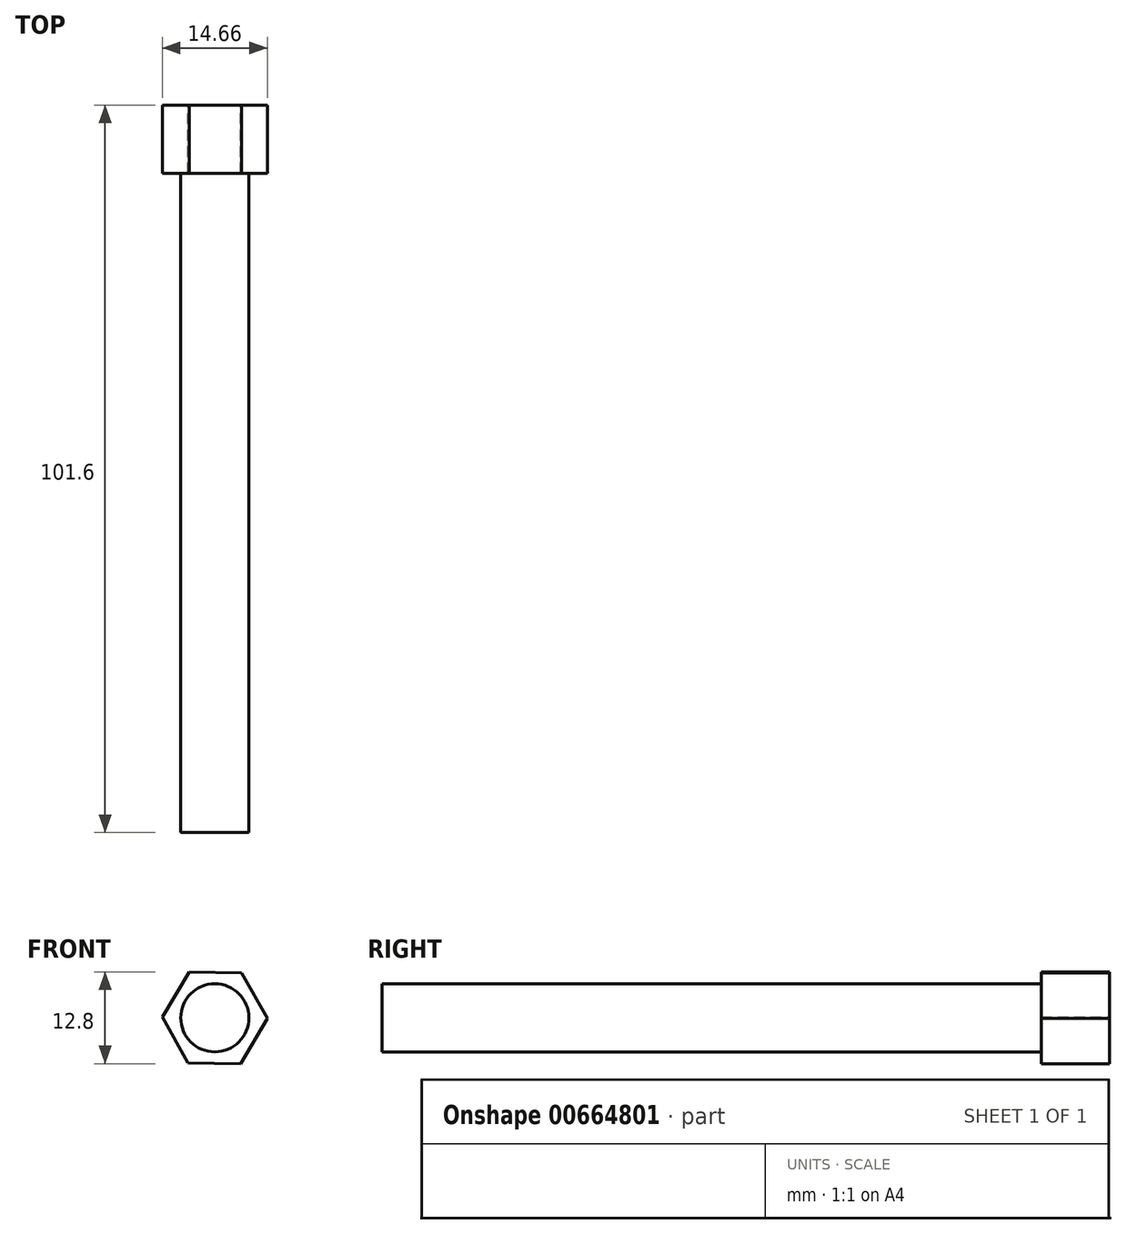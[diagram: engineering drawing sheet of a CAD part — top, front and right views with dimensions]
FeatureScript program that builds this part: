
annotation { "Feature Type Name" : "Feature", "Feature Type Description" : "" }
export const myFeature = defineFeature(function(context is Context, id is Id, definition is map)
    precondition{}
    {
        {
            var Q0;
            Q0=qCreatedBy(makeId("Front.planeOp"),FACE);
            var sketch = newSketch(context, id + "F0", { "sketchPlane" : qUnion([Q0])});
            skCircle(sketch, "E0", {"center": v(0, 0) * mm, "radius": 4.76 * mm});
            skSolve(sketch);
        }
        {
            var Q0;
            Q0=qCreatedBy(makeId("Front.planeOp"),FACE);
            var sketch = newSketch(context, id + "F1", { "sketchPlane" : qUnion([Q0])});
            skSolve(sketch);
        }
        {
            var Q0;
            Q0=makeQuery(id+"F0.imprint","IMPRINT",FACE,{"disambiguationData":[TD([[makeQuery(id+"F0.imprint","IMPRINT",EDGE,{"derivedFrom":sQuery(id+"F0.wireOp",EDGE,"E0")}),1.0]])]});
            var Q1;
            Q1 = qSketchRegion(id + "F1", true);
            extrude(context, id + "F2", {"entities" : qUnion([Q0, Q1]), "depth" : 101.6 * mm, "offsetDistance" : 25.4 * mm});
        }
        {
            var Q0;
            Q0=qCreatedBy(makeId("Front.planeOp"),FACE);
            var sketch = newSketch(context, id + "F3", { "sketchPlane" : qUnion([Q0])});
            skCircle(sketch, "E1.cCircle", {"center": v(0, 0) * mm, "radius": 6.35 * mm, "construction": true});
            skLineSegment(sketch, "E1.0", {"start": v(3.75, 6.3) * mm, "end": v(7.33, -0.1) * mm});
            skLineSegment(sketch, "E1.1", {"start": v(7.33, -0.1) * mm, "end": v(3.58, -6.4) * mm});
            skLineSegment(sketch, "E1.2", {"start": v(3.58, -6.4) * mm, "end": v(-3.75, -6.3) * mm});
            skLineSegment(sketch, "E1.3", {"start": v(-3.75, -6.3) * mm, "end": v(-7.33, 0.1) * mm});
            skLineSegment(sketch, "E1.4", {"start": v(-7.33, 0.1) * mm, "end": v(-3.58, 6.4) * mm});
            skLineSegment(sketch, "E1.5", {"start": v(-3.58, 6.4) * mm, "end": v(3.75, 6.3) * mm});
            skPoint(sketch, "E1.0.midPoint", {"position": v(5.54, 3.1) * mm});
            skSolve(sketch);
        }
        {
            var Q0;
            Q0=makeQuery(id+"F3.imprint","IMPRINT",FACE,{"disambiguationData":[TD([[makeQuery(id+"F3.imprint","IMPRINT",EDGE,{"derivedFrom":sQuery(id+"F3.wireOp",EDGE,"E1.0")}),-1.0]])]});
            extrude(context, id + "F4", {"entities" : qUnion([Q0]), "operationType" : NewBodyOperationType.ADD, "depth" : 9.52 * mm, "offsetDistance" : 25.4 * mm});
        }
    });
